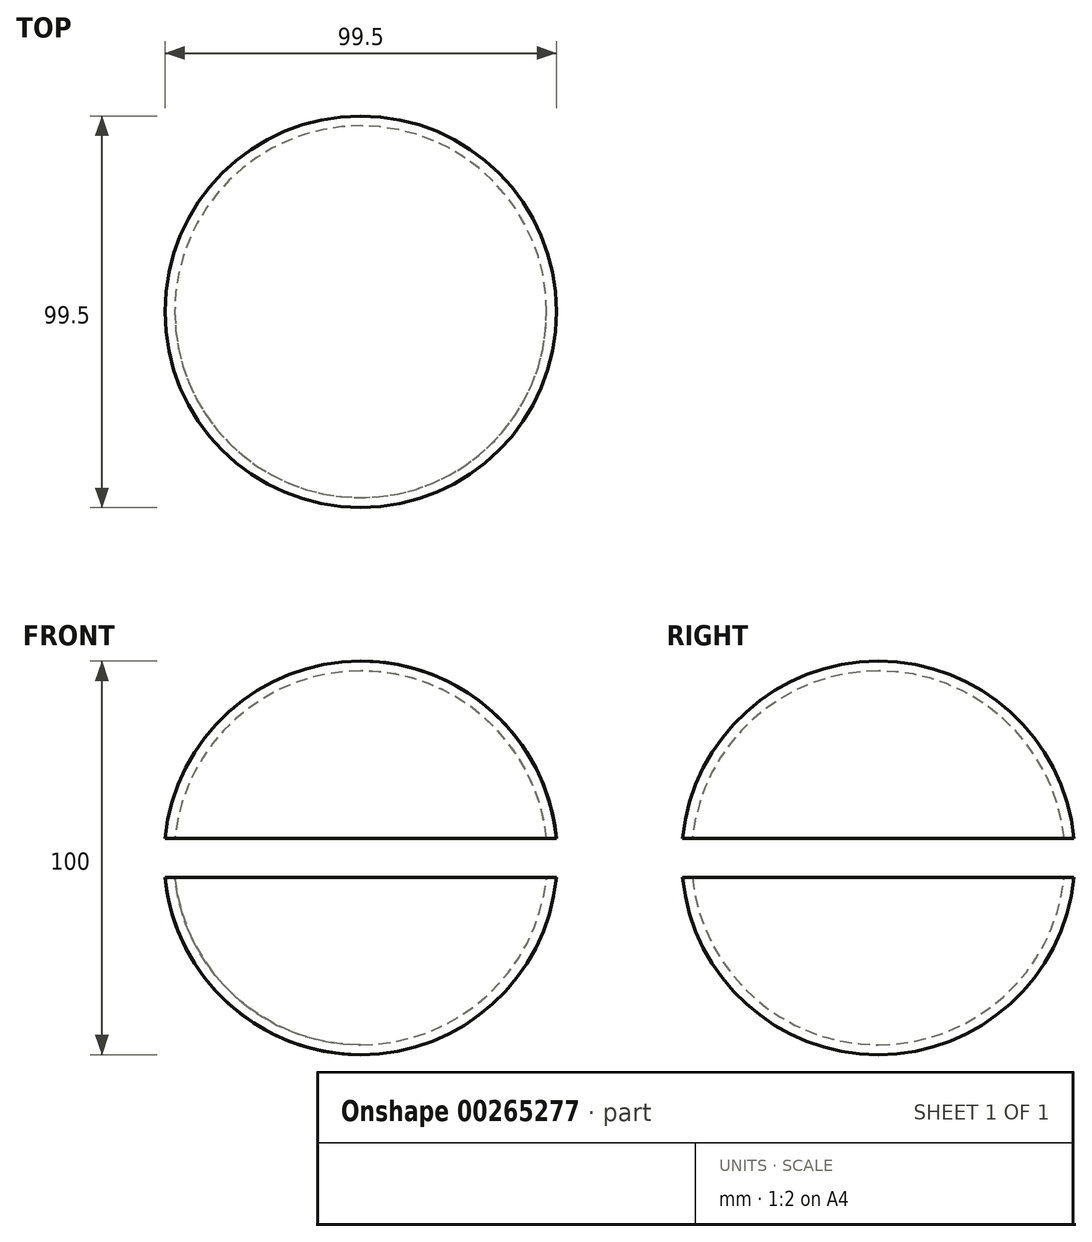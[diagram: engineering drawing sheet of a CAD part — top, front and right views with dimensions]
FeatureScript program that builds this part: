
annotation { "Feature Type Name" : "Feature", "Feature Type Description" : "" }
export const myFeature = defineFeature(function(context is Context, id is Id, definition is map)
    precondition{}
    {
        {
            var Q0;
            Q0=qCreatedBy(makeId("Top.planeOp"),FACE);
            var sketch = newSketch(context, id + "F0", { "sketchPlane" : qUnion([Q0])});
            skCircle(sketch, "E0", {"center": v(0, 0) * mm, "radius": 29.12 * mm});
            skSolve(sketch);
        }
        {
            var Q0;
            Q0=qCreatedBy(makeId("Front.planeOp"),FACE);
            var sketch = newSketch(context, id + "F1", { "sketchPlane" : qUnion([Q0])});
            skArc(sketch, "E1", {"start": v(0, -50) * mm, "mid": v(33.54, -37.08) * mm, "end": v(49.75, -5) * mm});
            skLineSegment(sketch, "E2", {"start": v(0, 50) * mm, "end": v(0, 5) * mm});
            skLineSegment(sketch, "E3", {"start": v(0, 5) * mm, "end": v(49.75, 5) * mm});
            skLineSegment(sketch, "E4", {"start": v(0, -5) * mm, "end": v(49.75, -5) * mm});
            skLineSegment(sketch, "E5.trimOffspring", {"start": v(0, -5) * mm, "end": v(0, -50) * mm});
            skArc(sketch, "E6.trimOffspring", {"start": v(49.75, 5) * mm, "mid": v(33.54, 37.08) * mm, "end": v(0, 50) * mm});
            skSolve(sketch);
        }
        {
            var Q0;
            Q0=makeQuery(id+"F1.imprint","IMPRINT",FACE,{"disambiguationData":[TD([[makeQuery(id+"F1.imprint","IMPRINT",EDGE,{"derivedFrom":sQuery(id+"F1.wireOp",EDGE,"E2")}),1.0]])]});
            var Q1;
            Q1=makeQuery(id+"F1.imprint","IMPRINT",FACE,{"disambiguationData":[TD([[makeQuery(id+"F1.imprint","IMPRINT",EDGE,{"derivedFrom":sQuery(id+"F1.wireOp",EDGE,"E1")}),1.0]])]});
            var Q2;
            Q2=sQuery(id+"F1.wireOp",EDGE,"E2");
            revolve(context, id + "F2", {"entities" : qUnion([Q0, Q1]), "axis" : qUnion([Q2]), "revolveType" : RevolveType.FULL});
        }
        {
            var Q0;
            Q0=makeQuery(id+"F2.opRevolve","SWEPT_FACE",FACE,{"disambiguationData":[OSD([sQuery(id+"F1.wireOp",EDGE,"E3")])]});
            var Q1;
            Q1=makeQuery(id+"F2.opRevolve","SWEPT_FACE",FACE,{"disambiguationData":[OSD([sQuery(id+"F1.wireOp",EDGE,"E4")])]});
            shell(context, id + "F3", {"entities" : qUnion([Q0, Q1]), "thickness" : 2.5 * mm});
        }
    });
